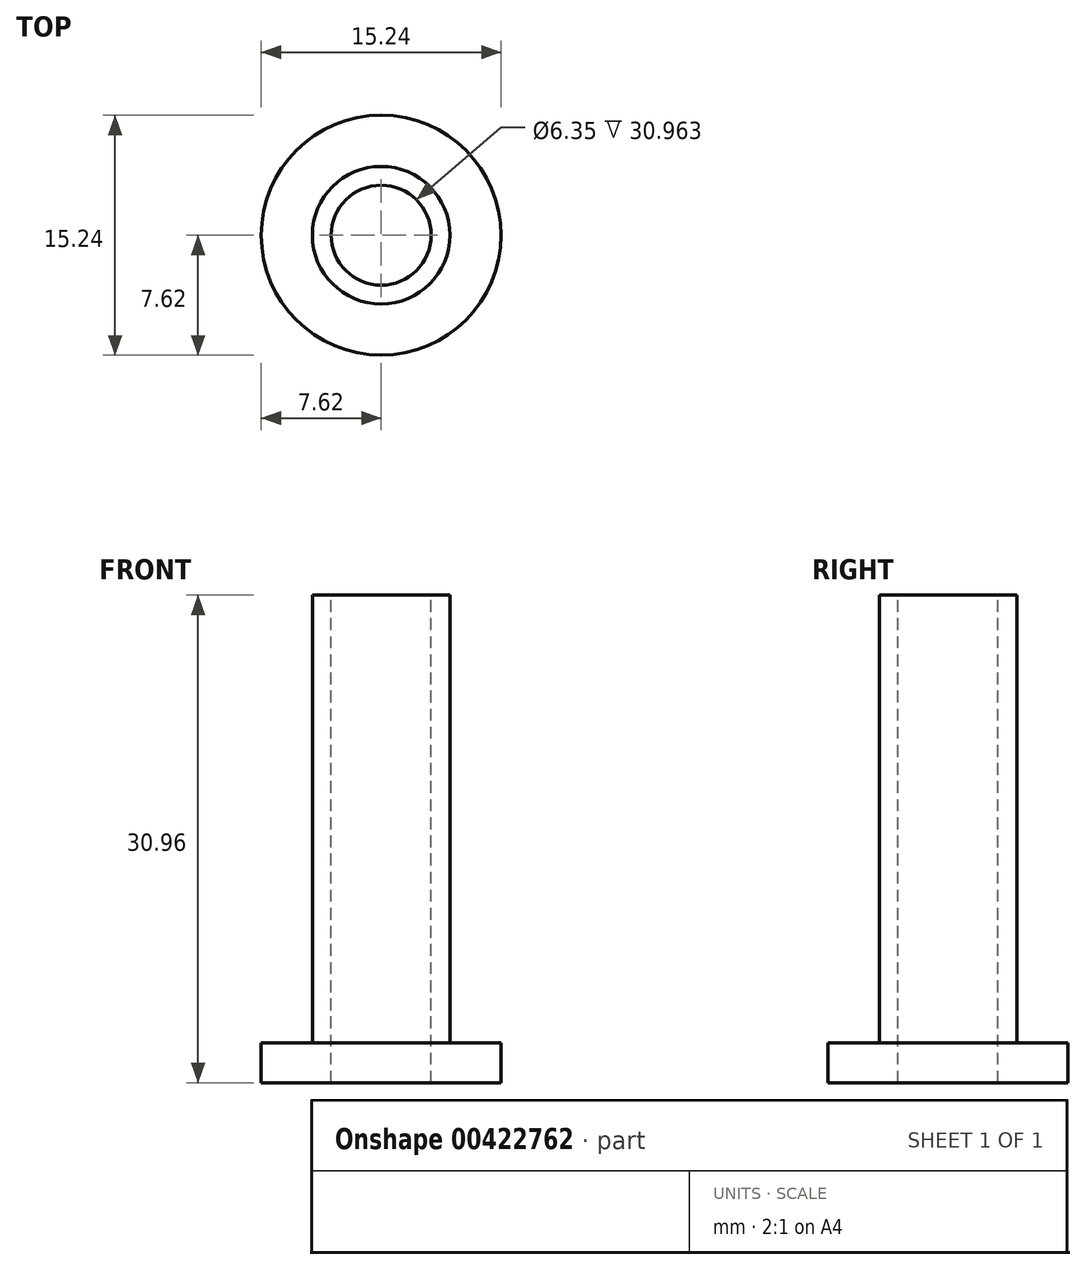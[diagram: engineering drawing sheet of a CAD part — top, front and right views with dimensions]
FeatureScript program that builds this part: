
annotation { "Feature Type Name" : "Feature", "Feature Type Description" : "" }
export const myFeature = defineFeature(function(context is Context, id is Id, definition is map)
    precondition{}
    {
        {
            var Q0;
            Q0=qCreatedBy(makeId("Top.planeOp"),FACE);
            var sketch = newSketch(context, id + "F0", { "sketchPlane" : qUnion([Q0])});
            skCircle(sketch, "E0", {"center": v(0, 0) * mm, "radius": 4.37 * mm});
            skCircle(sketch, "E1", {"center": v(0, 0) * mm, "radius": 7.62 * mm});
            skSolve(sketch);
        }
        {
            var Q0;
            Q0=makeQuery(id+"F0.imprint","IMPRINT",FACE,{"disambiguationData":[TD([[makeQuery(id+"F0.imprint","IMPRINT",EDGE,{"derivedFrom":sQuery(id+"F0.wireOp",EDGE,"e29fc86a-6ba9-40ce-92c8-c9a05fa3c3ab")}),1.0]])]});
            var Q1;
            Q1=makeQuery(id+"F0.imprint","IMPRINT",FACE,{"disambiguationData":[TD([[makeQuery(id+"F0.imprint","IMPRINT",EDGE,{"derivedFrom":sQuery(id+"F0.wireOp",EDGE,"E0")}),1.0]])]});
            extrude(context, id + "F1", {"entities" : qUnion([Q0, Q1]), "depth" : 28.42 * mm, "offsetDistance" : 25.4 * mm});
        }
        {
            var Q0;
            Q0=makeQuery(id+"F0.imprint","IMPRINT",FACE,{"disambiguationData":[TD([[makeQuery(id+"F0.imprint","IMPRINT",EDGE,{"derivedFrom":sQuery(id+"F0.wireOp",EDGE,"E0")}),-1.0]])]});
            var Q1;
            Q1=makeQuery(id+"F0.imprint","IMPRINT",FACE,{"disambiguationData":[TD([[makeQuery(id+"F0.imprint","IMPRINT",EDGE,{"derivedFrom":sQuery(id+"F0.wireOp",EDGE,"E0")}),1.0]])]});
            extrude(context, id + "F2", {"entities" : qUnion([Q0, Q1]), "operationType" : NewBodyOperationType.ADD, "oppositeDirection" : true, "depth" : 2.54 * mm, "offsetDistance" : 25.4 * mm});
        }
        {
            var Q0;
            Q0=makeQuery(id+"F1.opExtrude","CAP_FACE",FACE,{"disambiguationData":[OSD([sQuery(id+"F0.wireOp",EDGE,"E0")])],"isStart":false});
            var sketch = newSketch(context, id + "F3", { "sketchPlane" : qUnion([Q0])});
            skCircle(sketch, "E2", {"center": v(0, 0) * mm, "radius": 3.17 * mm});
            skSolve(sketch);
        }
        {
            var Q0;
            Q0=makeQuery(id+"F3.imprint","IMPRINT",FACE,{"disambiguationData":[TD([[makeQuery(id+"F3.imprint","IMPRINT",EDGE,{"derivedFrom":sQuery(id+"F3.wireOp",EDGE,"E2")}),1.0]])]});
            extrude(context, id + "F4", {"entities" : qUnion([Q0]), "operationType" : NewBodyOperationType.REMOVE, "endBound" : BoundingType.THROUGH_ALL, "oppositeDirection" : true, "depth" : 25.4 * mm, "offsetDistance" : 25.4 * mm});
        }
    });
